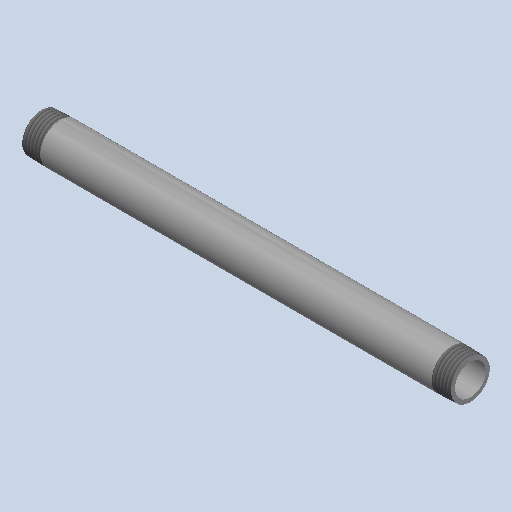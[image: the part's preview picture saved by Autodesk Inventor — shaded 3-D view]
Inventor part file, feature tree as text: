
AUTODESK INVENTOR PART (.ipt)
format: ipt  version: 2025 (Build 290162000, 162)  size: 182,784 bytes
history: native  units: mm (DEFAULTED — no unit token found)
features: other x8, revolve x1
ambient origin geometry x8: Origin, YZ Plane, XZ Plane, XY Plane, X Axis, Y Axis, Z Axis, Center Point
bodies: Solid1 (feature_tree)
feature tree (9):
  revolve  "Revolution1"  [1 undecoded]
  other  "Work Axis1"
  other  "Work Point5"
  other  "Work Axis2"
  other  "Work Point6"
  other  "Work Axis3"
  other  "Work Axis4"
  other  "Work Point7"
  other  "Work Point8"
note: 1 required parameter value undecoded (feature->parameter linkage not recoverable at this tier; creation-order binding heuristic only, values carry confidence <= 0.55)
